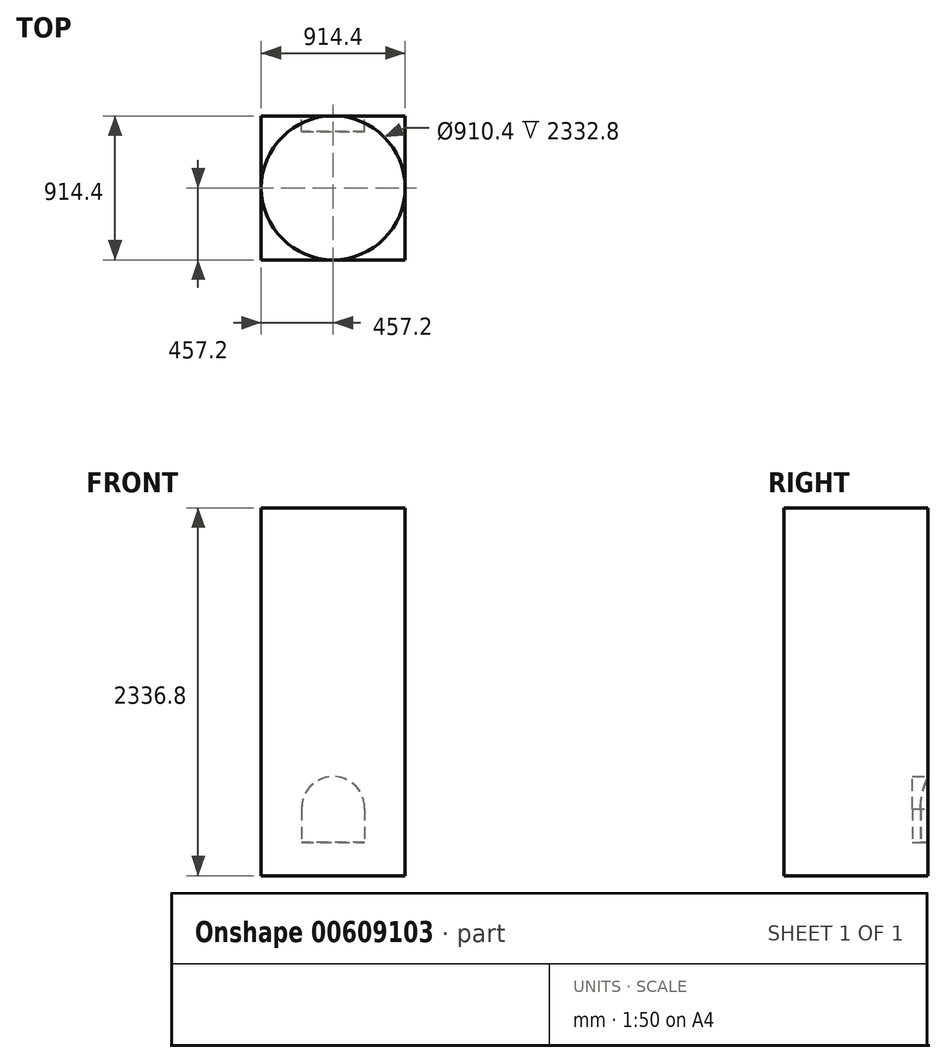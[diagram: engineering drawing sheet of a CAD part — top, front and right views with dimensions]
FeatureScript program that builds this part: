
annotation { "Feature Type Name" : "Feature", "Feature Type Description" : "" }
export const myFeature = defineFeature(function(context is Context, id is Id, definition is map)
    precondition{}
    {
        {
            var Q0;
            Q0=qCreatedBy(makeId("Top.planeOp"),FACE);
            var sketch = newSketch(context, id + "F0", { "sketchPlane" : qUnion([Q0])});
            skLineSegment(sketch, "E0.bottom", {"start": v(-457.2, 457.2) * mm, "end": v(457.2, 457.2) * mm});
            skLineSegment(sketch, "E0.top", {"start": v(-457.2, -457.2) * mm, "end": v(457.2, -457.2) * mm});
            skLineSegment(sketch, "E0.left", {"start": v(-457.2, 457.2) * mm, "end": v(-457.2, -457.2) * mm});
            skLineSegment(sketch, "E0.right", {"start": v(457.2, 457.2) * mm, "end": v(457.2, -457.2) * mm});
            skPoint(sketch, "E0.middle", {"position": v(0, 0) * mm});
            skSolve(sketch);
        }
        {
            var Q0;
            Q0=makeQuery(id+"F0.imprint","IMPRINT",FACE,{"disambiguationData":[TD([[makeQuery(id+"F0.imprint","IMPRINT",EDGE,{"derivedFrom":sQuery(id+"F0.wireOp",EDGE,"E0.bottom")}),-1.0]])]});
            extrude(context, id + "F1", {"entities" : qUnion([Q0]), "depth" : 2336.8 * mm, "offsetDistance" : 25 * mm});
        }
        {
            var Q0;
            Q0=qCreatedBy(makeId("Top.planeOp"),FACE);
            var sketch = newSketch(context, id + "F2", { "sketchPlane" : qUnion([Q0])});
            skCircle(sketch, "E1", {"center": v(0, 0) * mm, "radius": 457.2 * mm});
            skSolve(sketch);
        }
        {
            var Q0;
            Q0=makeQuery(id+"F2.imprint","IMPRINT",FACE,{"disambiguationData":[TD([[makeQuery(id+"F2.imprint","IMPRINT",EDGE,{"derivedFrom":sQuery(id+"F2.wireOp",EDGE,"E1")}),1.0]])]});
            extrude(context, id + "F3", {"entities" : qUnion([Q0]), "depth" : 2336.8 * mm, "offsetDistance" : 25 * mm});
        }
        {
            var Q0;
            Q0=makeQuery(id+"F3.opExtrude","SWEPT_FACE",FACE,{"disambiguationData":[OSD([sQuery(id+"F2.wireOp",EDGE,"E1")])]});
            var Q1;
            Q1=makeQuery(id+"F3.opExtrude","SWEPT_BODY",BODY,{"disambiguationData":[OSD([sQuery(id+"F2.wireOp",EDGE,"E1")])]});
            shell(context, id + "F4", {"isHollow" : true, "entities" : qUnion([Q0]), "parts" : qUnion([Q1]), "thickness" : 2 * mm});
        }
        {
            var Q0;
            Q0=makeQuery(id+"F1.opExtrude","SWEPT_FACE",FACE,{"disambiguationData":[OSD([sQuery(id+"F0.wireOp",EDGE,"E0.bottom")])]});
            var sketch = newSketch(context, id + "F5", { "sketchPlane" : qUnion([Q0])});
            skCircle(sketch, "E2", {"center": v(0, 429.45) * mm, "radius": 200 * mm});
            skLineSegment(sketch, "E3.bottom", {"start": v(-199.94, 424.7) * mm, "end": v(200.06, 424.7) * mm});
            skLineSegment(sketch, "E3.top", {"start": v(-199.94, 211.29) * mm, "end": v(200.06, 211.29) * mm});
            skLineSegment(sketch, "E3.left", {"start": v(-199.94, 424.7) * mm, "end": v(-199.94, 211.29) * mm});
            skLineSegment(sketch, "E3.right", {"start": v(200.06, 424.7) * mm, "end": v(200.06, 211.29) * mm});
            skSolve(sketch);
        }
        {
            var Q0;
            {var subQ0=sQuery(id+"F5.wireOp",EDGE,"E3.bottom");var subQ1=sQuery(id+"F5.wireOp",EDGE,"E2");var subQ3=makeQuery(id+"F5.imprint","INTERSECT",VERTEX,{"derivedFrom":[subQ1,subQ0]});Q0=makeQuery(id+"F5.imprint","IMPRINT",FACE,{"disambiguationData":[TD([[makeQuery(id+"F5.imprint","IMPRINT",EDGE,{"disambiguationData":[TD([[subQ3,-1.0]])],"derivedFrom":subQ1}),1.0]])]});}
            var Q1;
            {var subQ0=sQuery(id+"F5.wireOp",EDGE,"E3.bottom");var subQ1=sQuery(id+"F5.wireOp",EDGE,"E2");var subQ3=makeQuery(id+"F5.imprint","INTERSECT",VERTEX,{"derivedFrom":[subQ1,subQ0]});Q1=makeQuery(id+"F5.imprint","IMPRINT",FACE,{"disambiguationData":[TD([[makeQuery(id+"F5.imprint","IMPRINT",EDGE,{"disambiguationData":[TD([[subQ3,1.0]])],"derivedFrom":subQ1}),1.0]])]});}
            var Q2;
            Q2=makeQuery(id+"F5.imprint","IMPRINT",FACE,{"disambiguationData":[TD([[makeQuery(id+"F5.imprint","IMPRINT",EDGE,{"derivedFrom":sQuery(id+"F5.wireOp",EDGE,"E3.top")}),1.0]])]});
            extrude(context, id + "F6", {"entities" : qUnion([Q0, Q1, Q2]), "operationType" : NewBodyOperationType.REMOVE, "oppositeDirection" : true, "depth" : 25 * mm, "offsetDistance" : 25 * mm});
        }
        {
            var Q0;
            Q0=makeQuery(id+"F5.imprint","IMPRINT",FACE,{"disambiguationData":[TD([[makeQuery(id+"F5.imprint","IMPRINT",EDGE,{"derivedFrom":sQuery(id+"F5.wireOp",EDGE,"E3.top")}),1.0]])]});
            var Q1;
            {var subQ0=sQuery(id+"F5.wireOp",EDGE,"E3.bottom");var subQ1=sQuery(id+"F5.wireOp",EDGE,"E2");var subQ3=makeQuery(id+"F5.imprint","INTERSECT",VERTEX,{"derivedFrom":[subQ1,subQ0]});Q1=makeQuery(id+"F5.imprint","IMPRINT",FACE,{"disambiguationData":[TD([[makeQuery(id+"F5.imprint","IMPRINT",EDGE,{"disambiguationData":[TD([[subQ3,1.0]])],"derivedFrom":subQ1}),1.0]])]});}
            var Q2;
            {var subQ0=sQuery(id+"F5.wireOp",EDGE,"E3.bottom");var subQ1=sQuery(id+"F5.wireOp",EDGE,"E2");var subQ3=makeQuery(id+"F5.imprint","INTERSECT",VERTEX,{"derivedFrom":[subQ1,subQ0]});Q2=makeQuery(id+"F5.imprint","IMPRINT",FACE,{"disambiguationData":[TD([[makeQuery(id+"F5.imprint","IMPRINT",EDGE,{"disambiguationData":[TD([[subQ3,-1.0]])],"derivedFrom":subQ1}),1.0]])]});}
            extrude(context, id + "F7", {"entities" : qUnion([Q0, Q1, Q2]), "operationType" : NewBodyOperationType.REMOVE, "oppositeDirection" : true, "depth" : 100 * mm, "offsetDistance" : 25 * mm});
        }
    });
